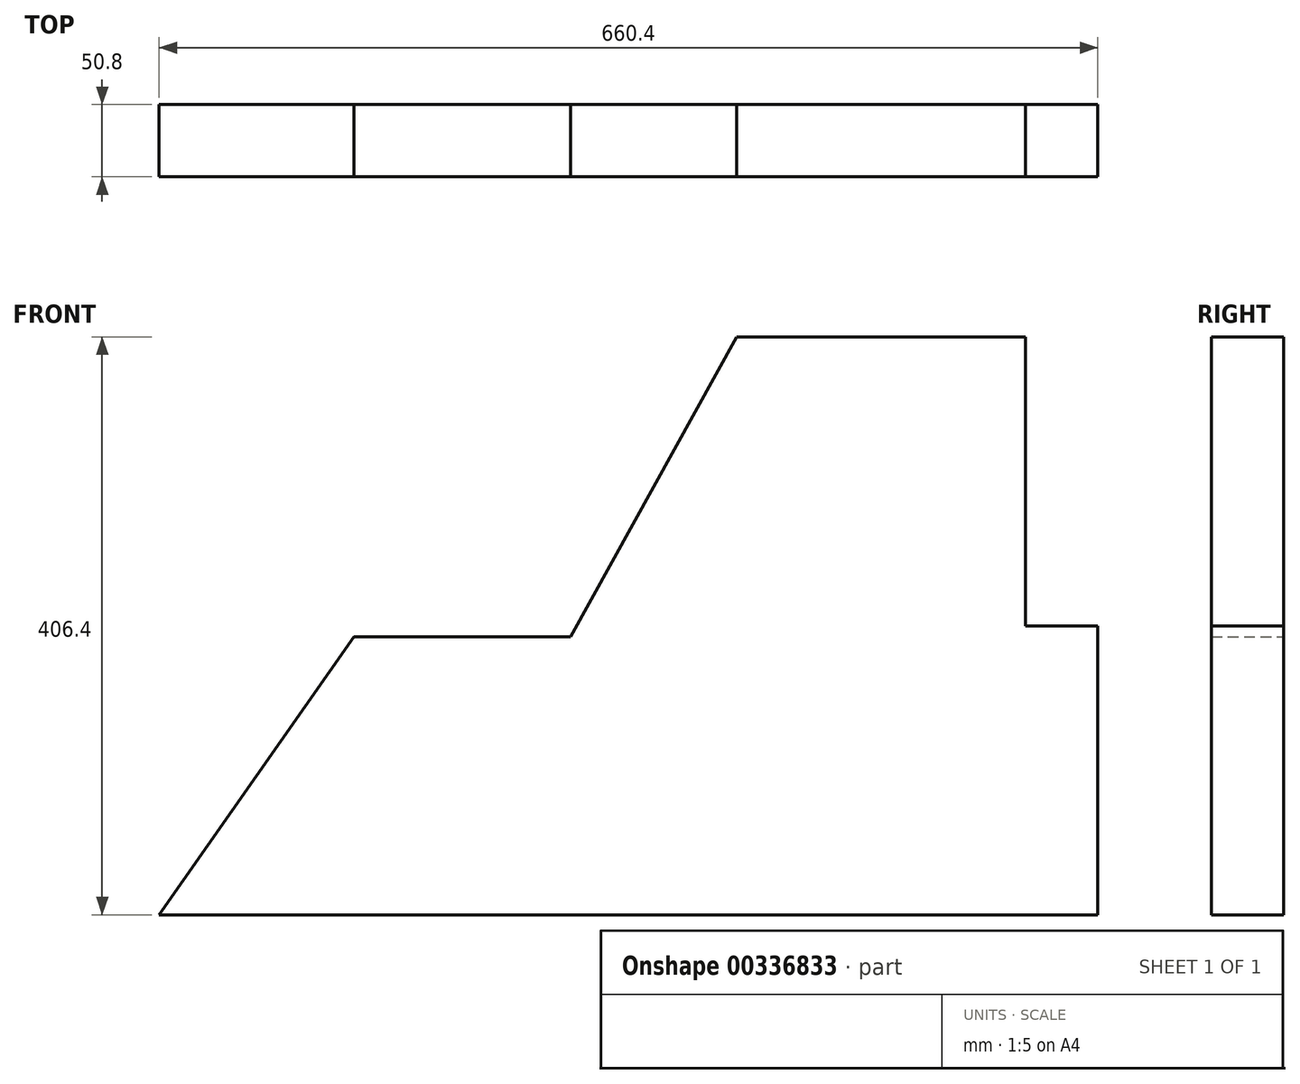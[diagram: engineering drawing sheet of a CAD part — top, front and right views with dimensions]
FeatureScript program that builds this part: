
annotation { "Feature Type Name" : "Feature", "Feature Type Description" : "" }
export const myFeature = defineFeature(function(context is Context, id is Id, definition is map)
    precondition{}
    {
        {
            var Q0;
            Q0=qCreatedBy(makeId("Front.planeOp"),FACE);
            var sketch = newSketch(context, id + "F0", { "sketchPlane" : qUnion([Q0])});
            skLineSegment(sketch, "E0", {"start": v(106.18, 252.16) * mm, "end": v(309.38, 252.16) * mm});
            skLineSegment(sketch, "E1", {"start": v(309.38, 252.16) * mm, "end": v(309.38, 48.96) * mm});
            skLineSegment(sketch, "E2", {"start": v(309.38, 48.96) * mm, "end": v(360.18, 48.96) * mm});
            skLineSegment(sketch, "E3", {"start": v(360.18, 48.96) * mm, "end": v(360.18, -154.24) * mm});
            skLineSegment(sketch, "E4", {"start": v(360.18, -154.24) * mm, "end": v(-300.22, -154.24) * mm});
            skLineSegment(sketch, "E5", {"start": v(-300.22, -154.24) * mm, "end": v(-163.06, 41.34) * mm});
            skLineSegment(sketch, "E6", {"start": v(-163.06, 41.34) * mm, "end": v(-10.66, 41.34) * mm});
            skLineSegment(sketch, "E7", {"start": v(-10.66, 41.34) * mm, "end": v(106.18, 252.16) * mm});
            skSolve(sketch);
        }
        {
            var Q0;
            Q0=makeQuery(id+"F0.imprint","IMPRINT",FACE,{"disambiguationData":[TD([[makeQuery(id+"F0.imprint","IMPRINT",EDGE,{"derivedFrom":sQuery(id+"F0.wireOp",EDGE,"E0")}),-1.0]])]});
            extrude(context, id + "F1", {"entities" : qUnion([Q0]), "depth" : 50.8 * mm});
        }
    });
